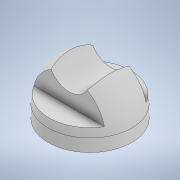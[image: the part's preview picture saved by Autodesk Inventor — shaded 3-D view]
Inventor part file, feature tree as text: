
AUTODESK INVENTOR PART (.ipt)
format: ipt  version: 2022 (Build 260153000, 153)  size: 136,704 bytes
history: native  units: mm
features: extrude x3, sketch x3, fillet x1
ambient origin geometry x8: Origin, YZ Plane, XZ Plane, XY Plane, X Axis, Y Axis, Z Axis, Center Point
bodies: Solid1 (feature_tree)
feature tree (7):
  extrude  "Extrusion1"  Depth=130.0mm TaperAngle=0.0deg
  fillet  "Fillet1"  Radius=100.0mm
  extrude  "Extrusion2"  Depth=100.0mm TaperAngle=0.0deg
  extrude  "Extrusion3"  Depth=50.0mm
  sketch  "Sketch1"  dims[d0=200.0mm d1=130.0mm d2=0.0mm d3=100.0mm]
  sketch  "Sketch2"  dims[d5=100.0mm d6=200.0mm d7=0.0mm]
  sketch  "Sketch3"  dims[d8=20.0mm d9=50.0mm d10=20.0mm d11=50.0mm d12=200.0mm d13=0.0mm d4=0.872665mm]
